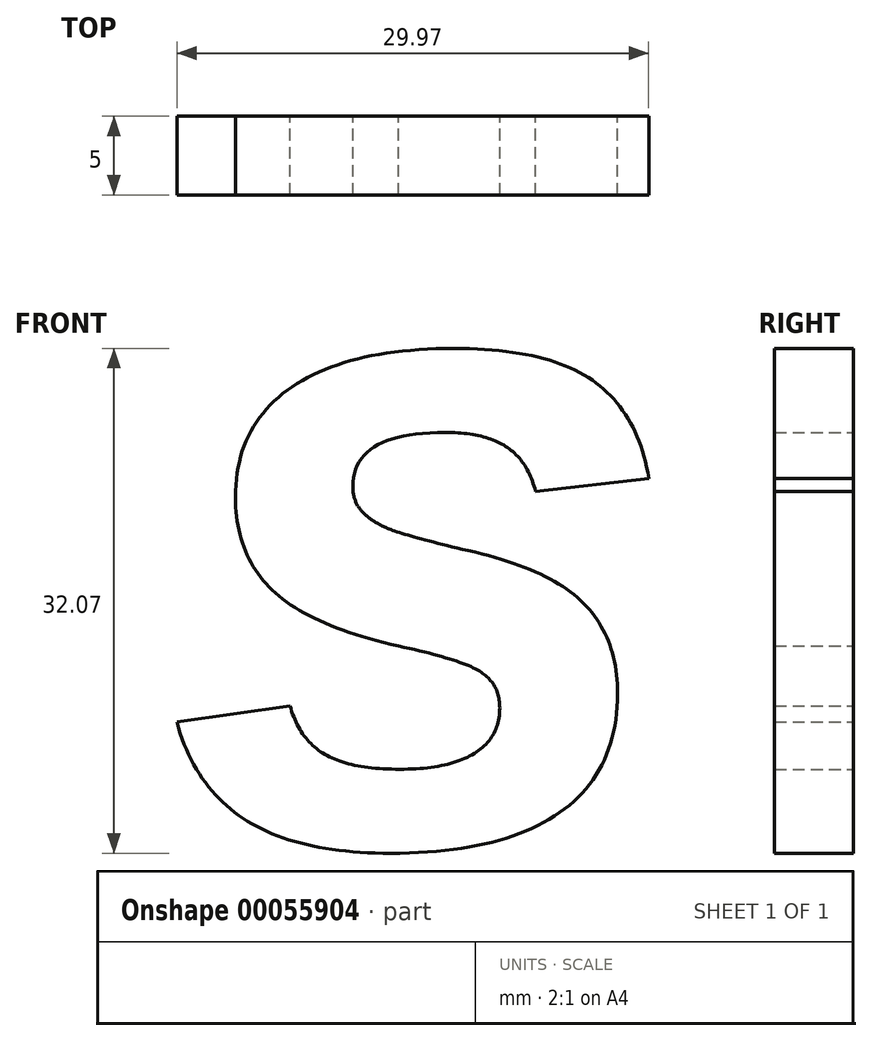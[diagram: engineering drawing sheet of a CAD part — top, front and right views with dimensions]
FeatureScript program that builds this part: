
annotation { "Feature Type Name" : "Feature", "Feature Type Description" : "" }
export const myFeature = defineFeature(function(context is Context, id is Id, definition is map)
    precondition{}
    {
        {
            var Q0;
            Q0=qCreatedBy(makeId("Front.planeOp"),FACE);
            var sketch = newSketch(context, id + "F0", { "sketchPlane" : qUnion([Q0])});
            skText(sketch, "E0", { "text": "s", "fontName": "Arimo-BoldItalic.ttf"});
            const initialGuessF0  = {"E0": [-0.06359, -0.00798, 1, 0, 0.04225]};
            skSetInitialGuess(sketch, initialGuessF0);
            skSolve(sketch);
        }
        {
            var Q0;
            Q0=makeQuery(id+"F0.imprint","IMPRINT",FACE,{"disambiguationData":[TD([[makeQuery(id+"F0.imprint","IMPRINT",EDGE,{"derivedFrom":sQuery(id+"F0.wireOp",EDGE,"E0.sketch_text.stroke-0")}),-1.0]])]});
            extrude(context, id + "F1", {"entities" : qUnion([Q0]), "depth" : 5 * mm});
        }
    });
